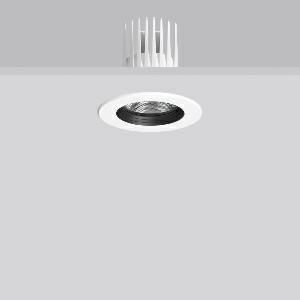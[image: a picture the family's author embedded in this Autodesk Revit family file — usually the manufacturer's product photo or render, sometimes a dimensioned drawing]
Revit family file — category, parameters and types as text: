
# Revit family: heledon_mini_e_901749_002_2_76_e158
name_source: partatom
category: Lighting Fixtures
units: mm (PartAtom-declared; Revit-internal decimal feet)

## family parameters
Cut with Voids When Loaded = No
Host = Face
Light Source = No
Part Type = Normal
Room Calculation Point = No
Round Connector Dimension = Use Diameter
Shared = No

## types (1)
- HELEDON mini E (1 x LED Modul 927, 3300 lm, 2700)
    Apparent Load = 29 VA
    Approval mark = CE
    CIE Flux Codes = 99 100 100 100 100
    Color Rendering = 92
    Color Temperature = 2700
    Default Elevation = 1800 mm
    Description = Series: HELEDON mini
Round recessed downlight. Housing: die-cast aluminium, powder-coated. Black plastic ring and recessed LED to prevent glare from the side. Optical assembly with reflector made of MIRO-Silver with 98% total light reflection for outstanding efficiency - can be changed without tools. Best colour rendering index Ra>90. Suitable for Recessed ceiling mounting. Installation without tools thanks to spring fastening system. Including separate LED converter with connecting cable 600 mm.High quality converter without flickering and stroboscopic effect. Through-wiring box (5 pole) available as accessory. The following accessories can be mounted without use of tools: interchangeable lenses, decorative glasses, honeycomb louvre, clear and frosted diffusers, white interchangeable plastic ring. 
Colour: traffic white, matt (RAL 9016)
Diameter: 124 mm
Height: 3 mm
Cut-out diameter: 114 mm
Recess height: 170 mm
Luminaire: recess height: 120 mm
Lamp: LED
Socket: without socket
Colour temperature: 2700K
Colour rendering index (CRI): 92
System power: 29 W
Rated luminous flux: 3300 lm
Luminous efficiency: 114 lm/W
Control gear: Converter, dimmable, DALI
Protection class: II
Type of protection: IP 20
    Height = 0 mm  [stored 0 ft]
    Lamp = 1 x LED Modul 927
    Lamp Light Flux = 3300 lm
    Lamp count = 1
    Length = 124 mm  [stored 0.406824 ft]
    Lifetime = 50000 h
    Luminous efficacy = 114 lm/W
    Manufacturer = RZB
    ModVariant = No
    Model = 901749.002.2.76
    Mounting Place = Ceiling
    Mounting Type = Recessed
    Number of Poles = 1
    OnlyDefault = Yes
    Power Factor = 1
    Product Name = HELEDON mini E
    Product group = Recessed downlights
    ProductGroupID = 402
    Protection Class = Protection class II
    Protection Degree = IP 20
    RLX_Detail_Level = 1
    RLX_Emergency_Light_Flux = 0 lm
    RLX_Emergency_Type = 0
    RLX_Emergency_Type_DB = No
    RlxData = <blob elided: 124965 chars, md5=3dca27ab>
    Socket = socket
    Standby Power = 0 W
    System Light Flux = 3300 lm
    System Power = 29 W
    Type Comments = Product without accessories
    Type Image = 901657.002.jpg
    URL = http://relux.com
    VarID = ---
    Voltage = 230 V
    Voltage Range = 220-240 V
    Weight = 0.00 kg
    Width = 0 mm  [stored 0 ft]

note: [stored X ft] marks values corroborated as IEEE doubles in the binary element streams (Revit-internal decimal feet)

## geometry (parser evidence)
native form markers: Blend x4, Sweep x12
no freeform markers — native parametric forms only
